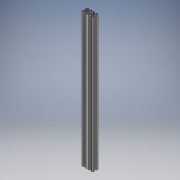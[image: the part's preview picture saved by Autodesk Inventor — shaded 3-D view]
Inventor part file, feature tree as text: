
AUTODESK INVENTOR PART (.ipt)
format: ipt  version: 2018 (Build 220112000, 112)  size: 577,024 bytes
history: native  units: mm
features: other x1, extrude x1, sketch x1
ambient origin geometry x8: Origin, YZ Plane, XZ Plane, XY Plane, X Axis, Y Axis, Z Axis, Center Point
bodies: Body1 (feature_tree)
feature tree (3):
  other  "Sólido1"
  extrude  "Extrusão1"  [1 undecoded]
  sketch  "Esboço1"  dims[d0=725.0mm d1=0.0mm]
note: 1 required parameter value undecoded (feature->parameter linkage not recoverable at this tier; creation-order binding heuristic only, values carry confidence <= 0.55)
